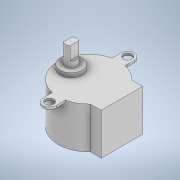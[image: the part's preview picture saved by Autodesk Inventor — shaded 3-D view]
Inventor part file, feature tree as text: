
AUTODESK INVENTOR PART (.ipt)
format: ipt  version: 2022 (Build 260153000, 153)  size: 160,768 bytes
history: native  units: mm
features: extrude x5, sketch x5, projected_geometry x1
ambient origin geometry x8: Origin, YZ Plane, XZ Plane, XY Plane, X Axis, Y Axis, Z Axis, Center Point
bodies: Solid1 (feature_tree)
feature tree (11):
  extrude  "Extrusion1"  Depth=19.0mm TaperAngle=0.0deg
  extrude  "Extrusion2"  Depth=19.0mm
  extrude  "Extrusion3"  Depth=3.9mm
  extrude  "Extrusion4"  Depth=1.0mm TaperAngle=0.0deg
  extrude  "Extrusion5"  Depth=6.0mm
  sketch  "Sketch1"  dims[d0=28.0mm d1=19.0mm d2=0.0mm]
  sketch  "Sketch2"  dims[d3=5.0mm d4=19.0mm]
  sketch  "Sketch3"  dims[d5=4.0mm d6=3.9mm]
  sketch  "Sketch4"  dims[d7=3.0mm d8=1.0mm d9=0.0mm]
  sketch  "Sketch5"  dims[d10=10.0mm d11=6.0mm d12=2.0mm d13=0.0mm d14=5.0mm d15=9.0mm d16=0.0mm d19=3.0mm d20=6.0mm d21=0.0mm]
  projected_geometry  "Projected Loop1"
